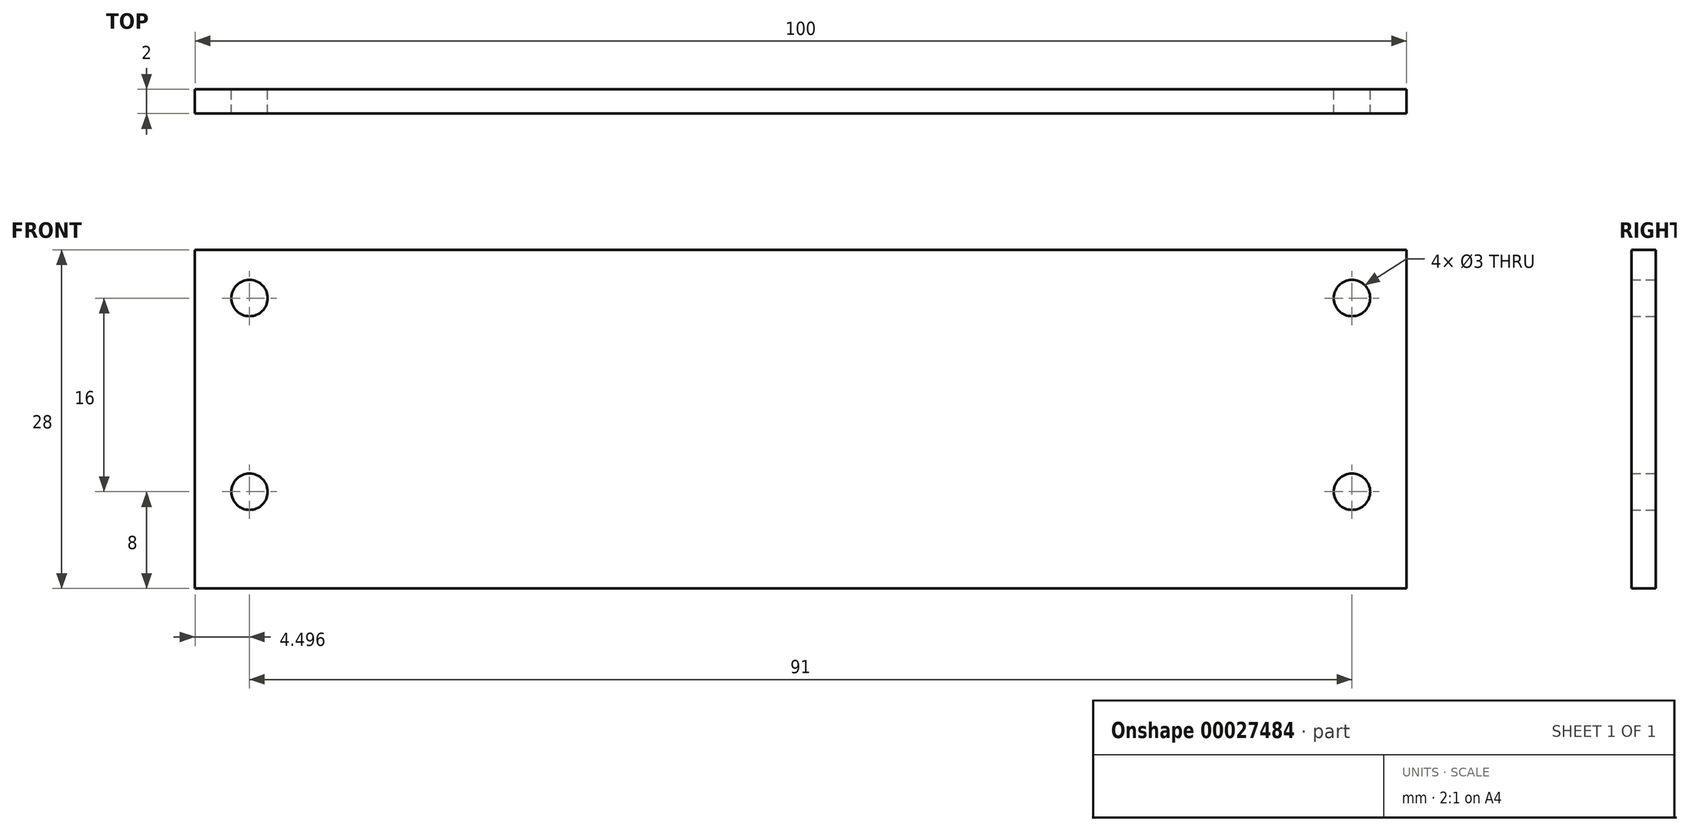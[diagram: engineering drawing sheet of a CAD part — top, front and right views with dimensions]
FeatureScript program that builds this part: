
annotation { "Feature Type Name" : "Feature", "Feature Type Description" : "" }
export const myFeature = defineFeature(function(context is Context, id is Id, definition is map)
    precondition{}
    {
        {
            var Q0;
            Q0=qCreatedBy(makeId("Front.planeOp"),FACE);
            var sketch = newSketch(context, id + "F0", { "sketchPlane" : qUnion([Q0])});
            skLineSegment(sketch, "E0.bottom", {"start": v(-26.81, 20) * mm, "end": v(73.19, 20) * mm});
            skLineSegment(sketch, "E0.top", {"start": v(-26.81, -8) * mm, "end": v(73.19, -8) * mm});
            skLineSegment(sketch, "E0.left", {"start": v(-26.81, 20) * mm, "end": v(-26.81, -8) * mm});
            skLineSegment(sketch, "E0.right", {"start": v(73.19, 20) * mm, "end": v(73.19, -8) * mm});
            skCircle(sketch, "E1", {"center": v(-22.31, 16) * mm, "radius": 1.5 * mm});
            skCircle(sketch, "E2", {"center": v(-22.31, 0) * mm, "radius": 1.5 * mm});
            skLineSegment(sketch, "E3", {"start": v(23.19, 20) * mm, "end": v(23.19, -8) * mm, "construction": true});
            skCircle(sketch, "E4.MirrorC", {"center": v(68.69, 16) * mm, "radius": 1.5 * mm});
            skCircle(sketch, "E5.MirrorC", {"center": v(68.69, 0) * mm, "radius": 1.5 * mm});
            skSolve(sketch);
        }
        {
            var Q0;
            Q0=makeQuery(id+"F0.imprint","IMPRINT",FACE,{"disambiguationData":[TD([[makeQuery(id+"F0.imprint","IMPRINT",EDGE,{"derivedFrom":sQuery(id+"F0.wireOp",EDGE,"E0.bottom")}),-1.0]])]});
            extrude(context, id + "F1", {"entities" : qUnion([Q0]), "depth" : 2 * mm});
        }
    });
